# Revit family: Electronics_Community_Biamp_Voice-Range-Horn-System_RSH-462
name_source: partatom
category: Communication Devices
units: mm (PartAtom-declared; Revit-internal decimal feet)

## family parameters
Cut with Voids When Loaded = No
Host = Face
Maintain Annotation Orientation = No
OmniClass Number = 23.85.10.11.14.14.14
Part Type = Normal
Room Calculation Point = No
Round Connector Dimension = Use Diameter
Shared = No

## types (1)
- RSH-462
    Axial DI = 14.4
    Axial Q = 27.5    1.6 to 4 kHz
    Axial Sensitivity (1W/1m) = 118 dB SPL (600 Hz to 4 kHz 1/3 octave bands);117 dB SPL (250 Hz to 4 kHz speech range)
    Connector Description = Terminal strip; 300W continuous, 750W program, 49 volts RMS, 110 volts momentary peak
    Construction = Hand laminated, reinforced composite fiberglass;Interior: Black gelcoat;Exterior: Grey gelcoat
    Default Elevation = 4' - 0"
    Depth = 1' - 10 1/2"
    Description = RSH-462 Voice-Range Exponential Focused Array Horn System with Mounting Bracket
    Drivers = 4 x M200 ferrofluid-cooled
    Environmental Performance = IEC529 IP66W rating with a minimum 5-degree downward aiming angle
    Height = 2' - 4 1/2"
    Housing Material = Biamp - Metal - Silver
    Loudspeaker Type = Exponential FocusedArray™ Horn System
    Manufacturer = Biamp
    Max Input Ratings = 300W continuous, 750W program;49 volts RMS, 110 volts momentary peak
    Maximum Output = 143 dB SPL / 150 dB SPL (peak)
    Minimum Impedance = 10.8 ohms @ 570 Hz
    Model = RSH-462
    Nominal Impedance = 11 ohms
    Nominal –6dB Beamwidth = 60°H (+1° / -4°, 1600 Hz to 4000 Hz);20°V (+20° / -0°, 1600 Hz to 4000 Hz)
    Operating Range = 400 Hz to 8 kHz;600 Hz to 4 kHz (± 4dB)
    Optional Accessories = Digital system processor
    Product Documentation Link = https://downloads.biamp.com
    Product Page URL = https://www.biamp.com
    Product data url = https://bimobject.com
    Recommended Power Amplifier = 630W to 900W @ 8 ohms
    Required Signal Processing = 400 Hz high pass filter (24 dB/Oct);8 kHz low pass filter (12 db/Oct);(for 4 x M200 driver standalone)
    Shipping Weight = 82.00 lb
    Supplied Accessories = Factory-installed mounting bracket, hot-dipped galvanized 304 stainless steel
    Throat Entrance Diameter = 4 x 2
    URL = https://www.biamp.com
    Usable LF Limit = 400 Hz
    Weight = 71.30 lb
    Width = 2' - 0 1/2"

## geometry (parser evidence)
native form markers: Sweep x5
no freeform markers — native parametric forms only
